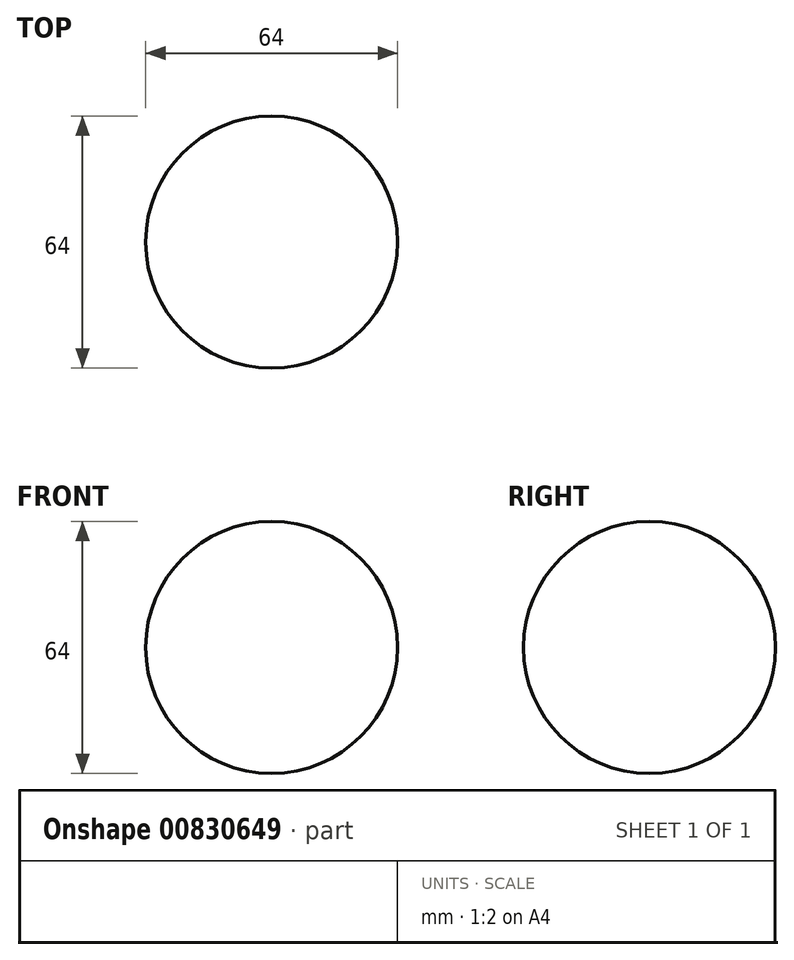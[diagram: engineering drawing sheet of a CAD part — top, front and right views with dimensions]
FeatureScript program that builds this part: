
annotation { "Feature Type Name" : "Feature", "Feature Type Description" : "" }
export const myFeature = defineFeature(function(context is Context, id is Id, definition is map)
    precondition{}
    {
        {
            var Q0;
            Q0=qCreatedBy(makeId("Front.planeOp"),FACE);
            var sketch = newSketch(context, id + "F0", { "sketchPlane" : qUnion([Q0])});
            skArc(sketch, "E0", {"start": v(0, -32) * mm, "mid": v(32, 0) * mm, "end": v(0, 32) * mm});
            skLineSegment(sketch, "E1", {"start": v(0, 32) * mm, "end": v(0, -32) * mm});
            skSolve(sketch);
        }
        {
            var Q0;
            Q0=makeQuery(id+"F0.imprint","IMPRINT",FACE,{"disambiguationData":[TD([[makeQuery(id+"F0.imprint","IMPRINT",EDGE,{"derivedFrom":sQuery(id+"F0.wireOp",EDGE,"E0")}),1.0]])]});
            var Q1;
            Q1=sQuery(id+"F0.wireOp",EDGE,"E1");
            revolve(context, id + "F1", {"surfaceOperationType" : NewSurfaceOperationType.NEW, "entities" : qUnion([Q0]), "axis" : qUnion([Q1]), "revolveType" : RevolveType.FULL});
        }
    });
